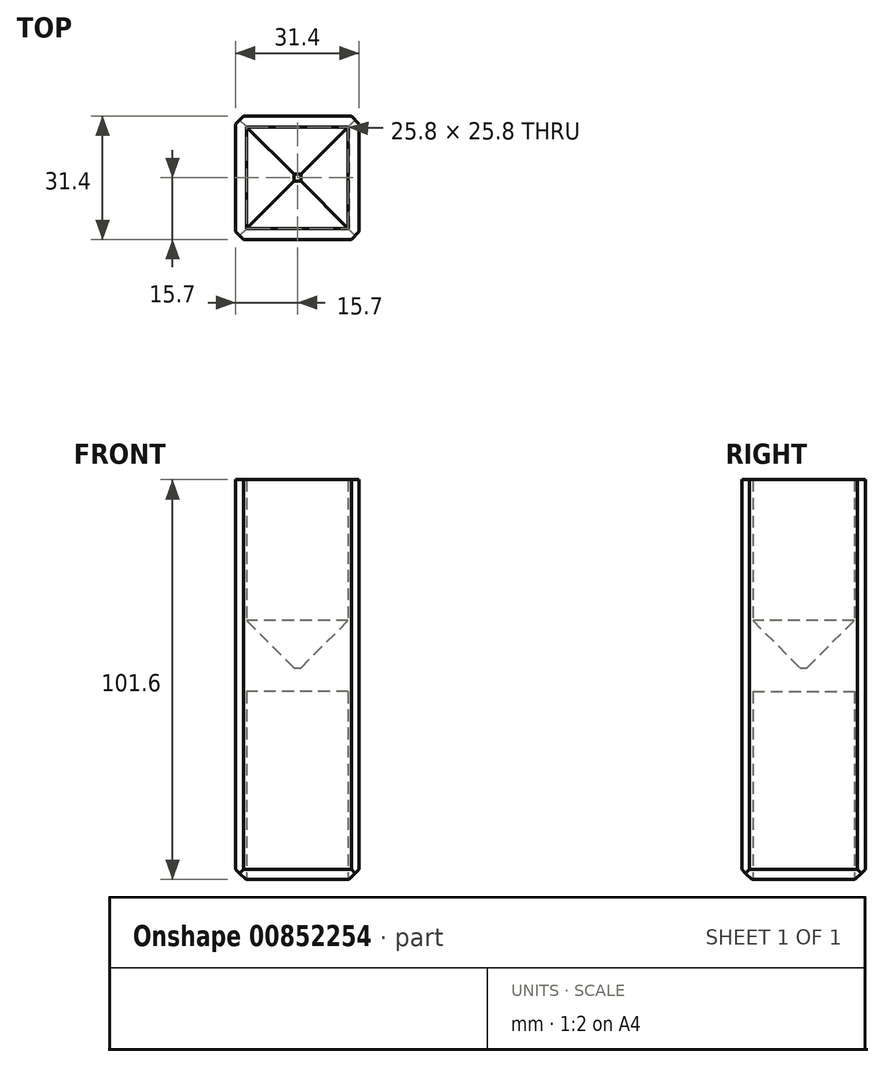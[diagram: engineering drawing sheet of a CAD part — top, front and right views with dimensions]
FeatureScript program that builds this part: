
annotation { "Feature Type Name" : "Feature", "Feature Type Description" : "" }
export const myFeature = defineFeature(function(context is Context, id is Id, definition is map)
    precondition{}
    {
        {
            var Q0;
            Q0=qCreatedBy(makeId("Top.planeOp"),FACE);
            var sketch = newSketch(context, id + "F0", { "sketchPlane" : qUnion([Q0])});
            skLineSegment(sketch, "E0.bottom", {"start": v(12.9, -12.9) * mm, "end": v(-12.9, -12.9) * mm});
            skLineSegment(sketch, "E0.top", {"start": v(12.9, 12.9) * mm, "end": v(-12.9, 12.9) * mm});
            skLineSegment(sketch, "E0.left", {"start": v(12.9, -12.9) * mm, "end": v(12.9, 12.9) * mm});
            skLineSegment(sketch, "E0.right", {"start": v(-12.9, -12.9) * mm, "end": v(-12.9, 12.9) * mm});
            skPoint(sketch, "E0.middle", {"position": v(0, 0) * mm});
            skLineSegment(sketch, "E1.bottom", {"start": v(15.7, -15.7) * mm, "end": v(-15.7, -15.7) * mm});
            skLineSegment(sketch, "E1.top", {"start": v(15.7, 15.7) * mm, "end": v(-15.7, 15.7) * mm});
            skLineSegment(sketch, "E1.left", {"start": v(15.7, -15.7) * mm, "end": v(15.7, 15.7) * mm});
            skLineSegment(sketch, "E1.right", {"start": v(-15.7, -15.7) * mm, "end": v(-15.7, 15.7) * mm});
            skSolve(sketch);
        }
        {
            var Q0;
            Q0 = qSketchRegion(id + "F0", true);
            extrude(context, id + "F1", {"entities" : qUnion([Q0]), "depth" : 50.8 * mm, "offsetDistance" : 25 * mm, "hasSecondDirection" : true, "secondDirectionOppositeDirection" : true, "secondDirectionDepth" : 50.8 * mm});
        }
        {
            var Q0;
            Q0=qCreatedBy(makeId("Top.planeOp"),FACE);
            var sketch = newSketch(context, id + "F2", { "sketchPlane" : qUnion([Q0])});
            skLineSegment(sketch, "E2.bottom", {"start": v(-14, 14) * mm, "end": v(14, 14) * mm});
            skLineSegment(sketch, "E2.top", {"start": v(-14, -14) * mm, "end": v(14, -14) * mm});
            skLineSegment(sketch, "E2.left", {"start": v(-14, 14) * mm, "end": v(-14, -14) * mm});
            skLineSegment(sketch, "E2.right", {"start": v(14, 14) * mm, "end": v(14, -14) * mm});
            skPoint(sketch, "E2.middle", {"position": v(0, 0) * mm});
            skSolve(sketch);
        }
        {
            var Q0;
            Q0 = qSketchRegion(id + "F2", true);
            extrude(context, id + "F3", {"entities" : qUnion([Q0]), "operationType" : NewBodyOperationType.ADD, "depth" : 3 * mm, "offsetDistance" : 25 * mm, "hasSecondDirection" : true, "secondDirectionOppositeDirection" : true, "secondDirectionDepth" : 3 * mm});
        }
        {
            var Q0;
            Q0=makeQuery(id+"F3.boolean.opBoolean","INTERSECT",EDGE,{"derivedFrom":[makeQuery(id+"F1.opExtrude","SWEPT_FACE",FACE,{"disambiguationData":[OSD([sQuery(id+"F0.wireOp",EDGE,"E0.top")])]}),makeQuery(id+"F3.opExtrude","CAP_FACE",FACE,{"disambiguationData":[OSD([sQuery(id+"F2.wireOp",EDGE,"E2.bottom"),sQuery(id+"F2.wireOp",EDGE,"E2.top"),sQuery(id+"F2.wireOp",EDGE,"E2.left"),sQuery(id+"F2.wireOp",EDGE,"E2.right")])],"isStart":false})]});
            var Q1;
            Q1=makeQuery(id+"F3.boolean.opBoolean","INTERSECT",EDGE,{"derivedFrom":[makeQuery(id+"F1.opExtrude","SWEPT_FACE",FACE,{"disambiguationData":[OSD([sQuery(id+"F0.wireOp",EDGE,"E0.left")])]}),makeQuery(id+"F3.opExtrude","CAP_FACE",FACE,{"disambiguationData":[OSD([sQuery(id+"F2.wireOp",EDGE,"E2.bottom"),sQuery(id+"F2.wireOp",EDGE,"E2.top"),sQuery(id+"F2.wireOp",EDGE,"E2.left"),sQuery(id+"F2.wireOp",EDGE,"E2.right")])],"isStart":false})]});
            var Q2;
            Q2=makeQuery(id+"F3.boolean.opBoolean","INTERSECT",EDGE,{"derivedFrom":[makeQuery(id+"F1.opExtrude","SWEPT_FACE",FACE,{"disambiguationData":[OSD([sQuery(id+"F0.wireOp",EDGE,"E0.bottom")])]}),makeQuery(id+"F3.opExtrude","CAP_FACE",FACE,{"disambiguationData":[OSD([sQuery(id+"F2.wireOp",EDGE,"E2.bottom"),sQuery(id+"F2.wireOp",EDGE,"E2.top"),sQuery(id+"F2.wireOp",EDGE,"E2.left"),sQuery(id+"F2.wireOp",EDGE,"E2.right")])],"isStart":false})]});
            var Q3;
            Q3=makeQuery(id+"F3.boolean.opBoolean","INTERSECT",EDGE,{"derivedFrom":[makeQuery(id+"F1.opExtrude","SWEPT_FACE",FACE,{"disambiguationData":[OSD([sQuery(id+"F0.wireOp",EDGE,"E0.right")])]}),makeQuery(id+"F3.opExtrude","CAP_FACE",FACE,{"disambiguationData":[OSD([sQuery(id+"F2.wireOp",EDGE,"E2.bottom"),sQuery(id+"F2.wireOp",EDGE,"E2.top"),sQuery(id+"F2.wireOp",EDGE,"E2.left"),sQuery(id+"F2.wireOp",EDGE,"E2.right")])],"isStart":false})]});
            chamfer(context, id + "F4", {"entities" : qUnion([Q0, Q1, Q2, Q3]), "width" : 12 * mm, "tangentPropagation" : true});
        }
        {
            var Q0;
            Q0=makeQuery(id+"F1.opExtrude","SWEPT_EDGE",EDGE,{"disambiguationData":[OSD([sQuery(id+"F0.wireOp",EDGE,"E1.bottom"),sQuery(id+"F0.wireOp",EDGE,"E1.left")])]});
            var Q1;
            Q1=makeQuery(id+"F1.opExtrude","SWEPT_EDGE",EDGE,{"disambiguationData":[OSD([sQuery(id+"F0.wireOp",EDGE,"E1.bottom"),sQuery(id+"F0.wireOp",EDGE,"E1.right")])]});
            var Q2;
            Q2=makeQuery(id+"F1.opExtrude","SWEPT_EDGE",EDGE,{"disambiguationData":[OSD([sQuery(id+"F0.wireOp",EDGE,"E1.top"),sQuery(id+"F0.wireOp",EDGE,"E1.left")])]});
            var Q3;
            Q3=makeQuery(id+"F1.opExtrude","SWEPT_EDGE",EDGE,{"disambiguationData":[OSD([sQuery(id+"F0.wireOp",EDGE,"E1.top"),sQuery(id+"F0.wireOp",EDGE,"E1.right")])]});
            chamfer(context, id + "F5", {"entities" : qUnion([Q0, Q1, Q2, Q3]), "width" : 2 * mm, "tangentPropagation" : true});
        }
        {
            var Q0;
            Q0=makeQuery(id+"F1.opExtrude","CAP_EDGE",EDGE,{"disambiguationData":[OSD([sQuery(id+"F0.wireOp",EDGE,"E1.left")])],"isStart":true});
            var Q1;
            Q1=makeQuery(id+"F1.opExtrude","CAP_EDGE",EDGE,{"disambiguationData":[OSD([sQuery(id+"F0.wireOp",EDGE,"E1.bottom")])],"isStart":true});
            var Q2;
            Q2=makeQuery(id+"F1.opExtrude","CAP_EDGE",EDGE,{"disambiguationData":[OSD([sQuery(id+"F0.wireOp",EDGE,"E1.right")])],"isStart":true});
            var Q3;
            Q3=makeQuery(id+"F1.opExtrude","CAP_EDGE",EDGE,{"disambiguationData":[OSD([sQuery(id+"F0.wireOp",EDGE,"E1.top")])],"isStart":true});
            chamfer(context, id + "F6", {"entities" : qUnion([Q0, Q1, Q2, Q3]), "width" : 2.6 * mm, "tangentPropagation" : true});
        }
    });
